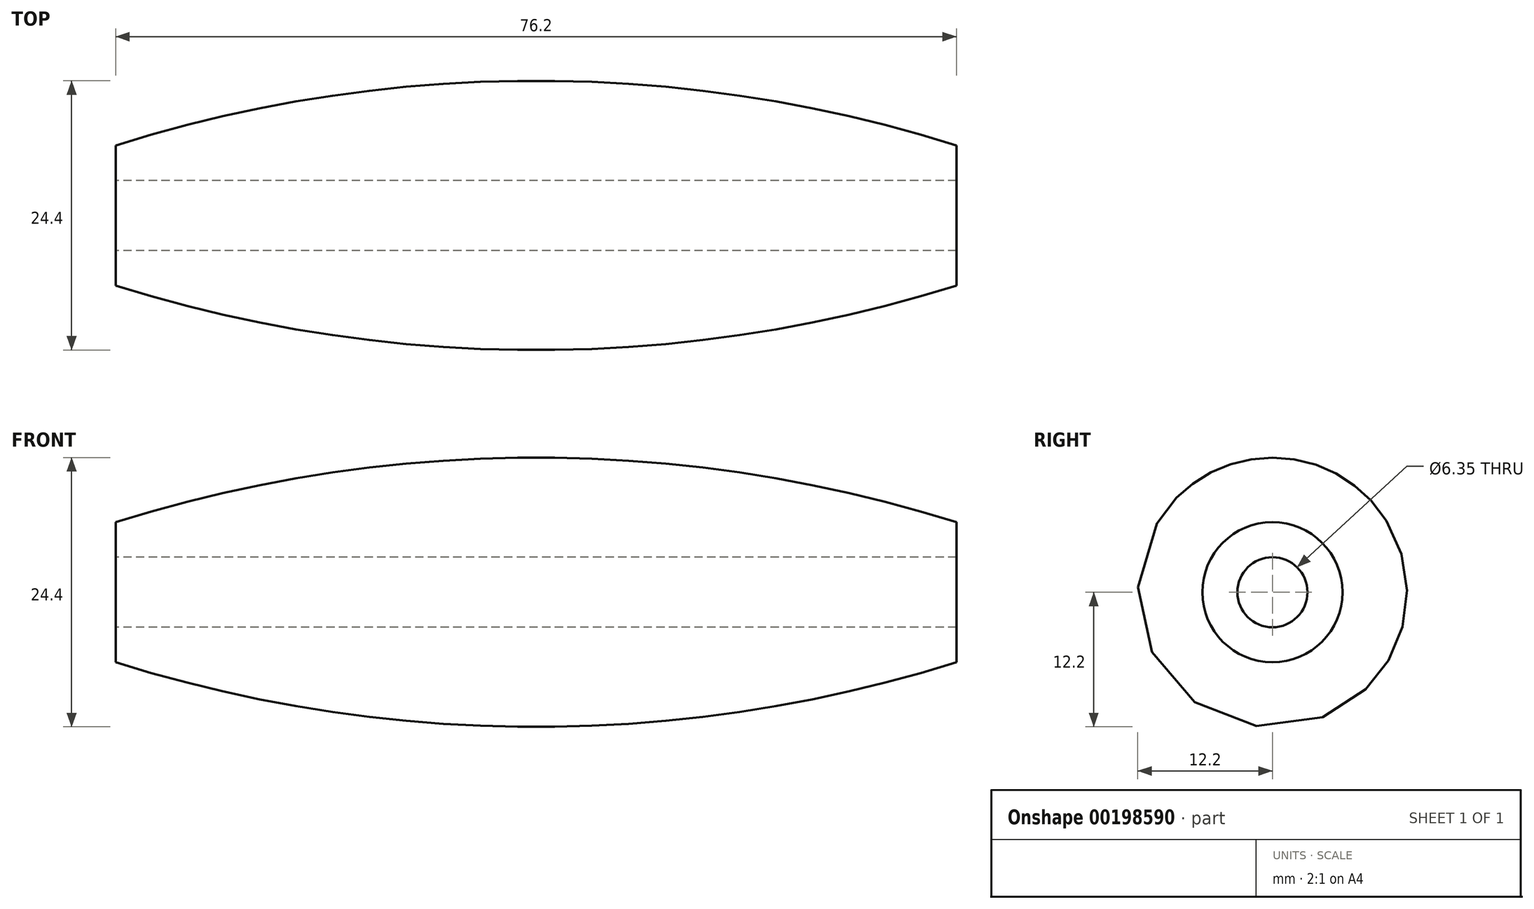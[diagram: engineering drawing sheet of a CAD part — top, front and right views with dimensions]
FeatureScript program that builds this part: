
annotation { "Feature Type Name" : "Feature", "Feature Type Description" : "" }
export const myFeature = defineFeature(function(context is Context, id is Id, definition is map)
    precondition{}
    {
        {
            var Q0;
            Q0=qCreatedBy(makeId("Front.planeOp"),FACE);
            var sketch = newSketch(context, id + "F0", { "sketchPlane" : qUnion([Q0])});
            skLineSegment(sketch, "E0", {"start": v(0, 0) * mm, "end": v(0, 3.18) * mm});
            skLineSegment(sketch, "E1", {"start": v(0, 3.18) * mm, "end": v(-38.1, 3.18) * mm});
            skLineSegment(sketch, "E2", {"start": v(0, 3.18) * mm, "end": v(38.1, 3.18) * mm});
            skLineSegment(sketch, "E3", {"start": v(38.1, 3.18) * mm, "end": v(38.1, 6.35) * mm});
            skLineSegment(sketch, "E4", {"start": v(-38.1, 3.18) * mm, "end": v(-38.1, 6.35) * mm});
            skArc(sketch, "E5", {"start": v(38.1, 6.35) * mm, "mid": v(0, 12.2) * mm, "end": v(-38.1, 6.35) * mm});
            skLineSegment(sketch, "E6", {"start": v(-48.08, 0) * mm, "end": v(44.17, 0) * mm});
            skSolve(sketch);
        }
        {
            var Q0;
            Q0 = qSketchRegion(id + "F0", true);
            var Q1;
            Q1=sQuery(id+"F0.wireOp",EDGE,"E6");
            revolve(context, id + "F1", {"entities" : qUnion([Q0]), "axis" : qUnion([Q1]), "revolveType" : RevolveType.FULL});
        }
    });
